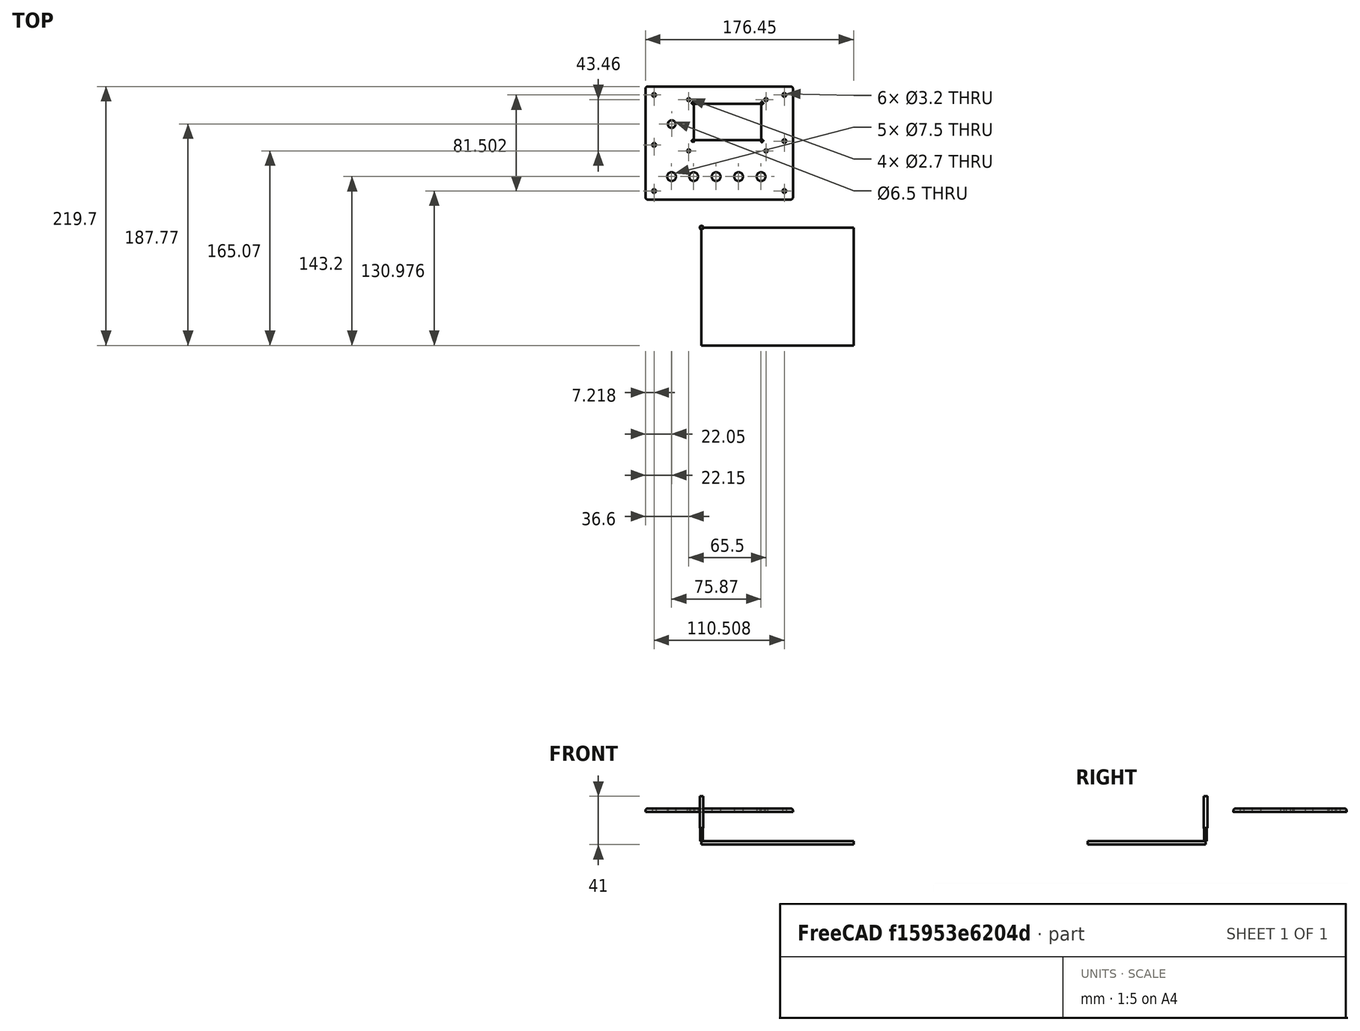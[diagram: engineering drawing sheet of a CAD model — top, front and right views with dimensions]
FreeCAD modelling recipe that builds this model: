
FCSTD DOCUMENT  (FreeCAD 0.21R33771 (Git))
Label: Top Plate CNC Job
License: All rights reserved
LicenseURL: http://en.wikipedia.org/wiki/All_rights_reserved
objects: Path::FeaturePython×5, Part::FeaturePython×3, App::DocumentObjectGroup×3, Part::Feature×1, App::Part×1, App::FeaturePython×1
note: 7 computed .brp shape members not serialized (recipe doc carries the construction recipe); baked Part::Feature solids carry a one-line shape summary decoded from their .brp

FEATURE [Part::Feature] Part__Feature  label="Top Plate"
  Placement = pos=(0,0,24.7) rot=(0,0,1;0rad)
  shape: bbox 125 x 96 x 3 mm, 50 faces (baked)
FEATURE [App::Part] Top_Enclosure_Plate  label="Top Enclosure Plate"
  Group = -> [Part__Feature]
  Origin = -> Origin
FEATURE [App::FeaturePython] SetupSheet  # Path/CAM operation (typed FeaturePython)
  ClearanceHeightExpression = OpStockZMax+SetupSheet.ClearanceHeightOffset
  ClearanceHeightOffset = 5
  CoolantMode = 0
  CoolantModes = None | Flood | Mist
  FinalDepthExpression = OpFinalDepth
  HorizRapid = 0
  SafeHeightExpression = OpStockZMax+SetupSheet.SafeHeightOffset
  SafeHeightOffset = 3
  StartDepthExpression = OpStartDepth
  StepDownExpression = OpToolDiameter
  VertRapid = 0
FEATURE [Part::FeaturePython] Clone  label="Model-Top Enclosure Plate"  # Draft clone (typed FeaturePython)
  AttacherType = Attacher::AttachEngine3D
  Fuse = false
  Objects = -> [Top_Enclosure_Plate]
  PathResource = Model
  Placement = pos=(49.4504,-121.7,-27.7) rot=(0,0,1;0rad)
  Scale = (1,1,1)
FEATURE [App::DocumentObjectGroup] Model
  Group = -> [Clone]
FEATURE [Part::FeaturePython] ToolBit  label="Endmill"  # Path/CAM toolbit (typed FeaturePython)
  BitPropertyNames = Chipload | CuttingEdgeHeight | Diameter | Flutes | Length | Material | ShankDiameter | SpindleDirection
  BitShape = C:/Program Files/FreeCAD 0.21/Mod\Path\Tools\Shape\endmill.fcstd
  Chipload = 0
  CuttingEdgeHeight = 11
  Diameter = 2
  Flutes = 0
  Length = 38
  Material = 0
  ShankDiameter = 3.1
  ShapeName = endmill
  SpindleDirection = 0
FEATURE [Path::FeaturePython] TC__Default_Tool  label="TC: EndMill01"  # Path/CAM operation (typed FeaturePython)
  HorizFeed = 5
  HorizRapid = 0
  SpindleDir = 0
  SpindleSpeed = 10000
  Tool = -> ToolBit
  ToolNumber = 10
  VertFeed = 2
  VertRapid = 0
  expr: HorizRapid = SetupSheet.HorizRapid
  expr: VertRapid = SetupSheet.VertRapid
FEATURE [App::DocumentObjectGroup] Tools
  Group = -> [TC__Default_Tool]
FEATURE [Part::FeaturePython] Stock001  # WARN: FeaturePython — macro-defined, semantics opaque (R4)
  Height = 3
  Length = 129
  Placement = pos=(0,-100,-3) rot=(0,0,1;0rad)
  StockType = CreateBox
  Width = 100
FEATURE [Path::FeaturePython] Pocket_Shape  label="Mounting & Bolt Holes"  # Path/CAM operation (typed FeaturePython)
  Active = true
  AreaParams:
    Tolerance = 1e-07
    FitArcs = True
    Simplify = False
    CleanDistance = 0.0
    Accuracy = 0.01
    Unit = 1.0
    MinArcPoints = 4
    MaxArcPoints = 100
    ClipperScale = 10000000.0
    Fill = 0
    Coplanar = 0
    Reorient = True
    Outline = False
    Explode = False
    OpenMode = 0
    Deflection = 0.01
    SubjectFill = 0
    ClipFill = 0
    Offset = 0.0
    ExtraPass = 0
    Stepover = 0.0
    LastStepover = 0.0
    JoinType = 0
    EndType = 0
    MiterLimit = 2.0
    RoundPrecision = 0.0
    PocketMode = 2
    ToolRadius = 1.0
    PocketExtraOffset = 0.0
    PocketStepover = 1.0
    PocketLastStepover = 0.0
    FromCenter = True
    Angle = 45.0
    AngleShift = 0.0
    Shift = 0.0
    Thicken = False
    SectionCount = -1
    Stepdown = 1.0
    SectionOffset = 0.0
    SectionTolerance = 1e-07
    SectionMode = 2
    Project = False
  Base = -> [Clone]
  ClearanceHeight = 5
  CoolantMode = 0
  CutMode = 0
  CycleTime = 00:10:06
  ExtensionCorners = true
  ExtensionLengthDefault = 1
  ExtraOffset = 0
  FinalDepth = -3
  FinishDepth = 0
  KeepToolDown = false
  MinTravel = false
  OffsetPattern = 1
  OpFinalDepth = -3
  OpStartDepth = 0
  OpStockZMax = 0
  OpStockZMin = -3
  OpToolDiameter = 2
  PathParams = {'orientation': 1, 'feedrate': 5.0, 'feedrate_v': 2.0, 'verbose': True, 'resume_height': 3.0, 'retraction': 5.0, 'return_end': True, 'preamble': False, 'start': Vector (119.15039579599825, -9.379392316911378, 5.0)}
  PocketLastStepOver = 0
  SafeHeight = 3
  SplitArcs = false
  StartAt = 0
  StartDepth = 0
  StartPoint = (0,0,0)
  StepDown = 2
  StepOver = 50
  ToolController = -> TC__Default_Tool
  UseOutline = false
  UseStartPoint = false
  ZigZagAngle = 45
  expr: ClearanceHeight = OpStockZMax + SetupSheet.ClearanceHeightOffset
  expr: ExtensionLengthDefault = OpToolDiameter / 2
  expr: FinalDepth = OpFinalDepth
  expr: SafeHeight = OpStockZMax + SetupSheet.SafeHeightOffset
  expr: StartDepth = OpStartDepth
  expr: StepDown = OpToolDiameter
FEATURE [Path::FeaturePython] Pocket_Shape001  label="Display Pocket"  # Path/CAM operation (typed FeaturePython)
  Active = true
  AreaParams:
    Tolerance = 1e-07
    FitArcs = True
    Simplify = False
    CleanDistance = 0.0
    Accuracy = 0.01
    Unit = 1.0
    MinArcPoints = 4
    MaxArcPoints = 100
    ClipperScale = 10000000.0
    Fill = 0
    Coplanar = 0
    Reorient = True
    Outline = False
    Explode = False
    OpenMode = 0
    Deflection = 0.01
    SubjectFill = 0
    ClipFill = 0
    Offset = 0.0
    ExtraPass = 0
    Stepover = 0.0
    LastStepover = 0.0
    JoinType = 0
    EndType = 0
    MiterLimit = 2.0
    RoundPrecision = 0.0
    PocketMode = 2
    ToolRadius = 1.0
    PocketExtraOffset = 0.0
    PocketStepover = 1.0
    PocketLastStepover = 0.0
    FromCenter = True
    Angle = 45.0
    AngleShift = 0.0
    Shift = 0.0
    Thicken = False
    SectionCount = -1
    Stepdown = 1.0
    SectionOffset = 0.0
    SectionTolerance = 1e-07
    SectionMode = 2
    Project = False
  Base = -> [Clone]
  ClearanceHeight = 5
  CoolantMode = 0
  CutMode = 0
  CycleTime = 00:15:16
  ExtensionCorners = true
  ExtensionLengthDefault = 1
  ExtraOffset = 0
  FinalDepth = -3
  FinishDepth = 0
  KeepToolDown = false
  MinTravel = false
  OffsetPattern = 1
  OpFinalDepth = -3
  OpStartDepth = 0
  OpStockZMax = 0
  OpStockZMin = -3
  OpToolDiameter = 2
  PathParams = {'orientation': 1, 'feedrate': 5.0, 'feedrate_v': 2.0, 'verbose': True, 'resume_height': 3.0, 'retraction': 5.0, 'return_end': True, 'preamble': False}
  PocketLastStepOver = 0
  SafeHeight = 3
  SplitArcs = false
  StartAt = 0
  StartDepth = 0
  StartPoint = (0,0,0)
  StepDown = 2
  StepOver = 50
  ToolController = -> TC__Default_Tool
  UseOutline = false
  UseStartPoint = false
  ZigZagAngle = 45
  expr: ClearanceHeight = OpStockZMax + SetupSheet.ClearanceHeightOffset
  expr: ExtensionLengthDefault = OpToolDiameter / 2
  expr: FinalDepth = OpFinalDepth
  expr: SafeHeight = OpStockZMax + SetupSheet.SafeHeightOffset
  expr: StartDepth = OpStartDepth
  expr: StepDown = OpToolDiameter
FEATURE [Path::FeaturePython] Profile  # Path/CAM operation (typed FeaturePython)
  Active = true
  AreaParams:
    Tolerance = 1e-07
    FitArcs = True
    Simplify = False
    CleanDistance = 0.0
    Accuracy = 0.01
    Unit = 1.0
    MinArcPoints = 4
    MaxArcPoints = 100
    ClipperScale = 10000000.0
    Fill = 0
    Coplanar = 0
    Reorient = True
    Outline = False
    Explode = False
    OpenMode = 0
    Deflection = 0.01
    SubjectFill = 0
    ClipFill = 0
    Offset = 1.0
    ExtraPass = 0
    Stepover = 0.0
    LastStepover = 0.0
    JoinType = 0
    EndType = 0
    MiterLimit = 2.0
    RoundPrecision = 0.0
    PocketMode = 0
    ToolRadius = 1.0
    PocketExtraOffset = 0.0
    PocketStepover = 0.0
    PocketLastStepover = 0.0
    FromCenter = False
    Angle = 45.0
    AngleShift = 0.0
    Shift = 0.0
    Thicken = False
    SectionCount = -1
    Stepdown = 1.0
    SectionOffset = 0.0
    SectionTolerance = 1e-07
    SectionMode = 2
    Project = False
  Base = -> [Clone]
  ClearanceHeight = 5
  CoolantMode = 0
  CycleTime = 00:03:32
  Direction = 0
  FinalDepth = -3
  HandleMultipleFeatures = 0
  JoinType = 0
  MiterLimit = 0.1
  OffsetExtra = 0
  OpFinalDepth = -3
  OpStartDepth = 0
  OpStockZMax = 0
  OpStockZMin = -3
  OpToolDiameter = 2
  PathParams = {'orientation': 1, 'feedrate': 5.0, 'feedrate_v': 2.0, 'verbose': True, 'resume_height': 3.0, 'retraction': 5.0, 'return_end': True, 'preamble': False}
  SafeHeight = 3
  Side = 0
  SplitArcs = false
  StartDepth = 0
  StartPoint = (0,0,0)
  StepDown = 2
  ToolController = -> TC__Default_Tool
  UseComp = true
  UseStartPoint = false
  processCircles = false
  processHoles = false
  processPerimeter = true
  expr: ClearanceHeight = OpStockZMax + SetupSheet.ClearanceHeightOffset
  expr: FinalDepth = OpFinalDepth
  expr: SafeHeight = OpStockZMax + SetupSheet.SafeHeightOffset
  expr: StartDepth = OpStartDepth
  expr: StepDown = OpToolDiameter
FEATURE [App::DocumentObjectGroup] Operations
  Group = -> [Pocket_Shape,Pocket_Shape001,Profile]
FEATURE [Path::FeaturePython] Job  # Path/CAM operation (typed FeaturePython)
  CycleTime = 00:28:54
  Fixtures = G54
  GeometryTolerance = 0.01
  JobType = 0
  LastPostProcessDate = 2024-08-13 14:29:16.978612
  LastPostProcessOutput = <userpath>\OneDrive\Github-projects\ElectricGuitarMK1\Research and Development\Interface Section\AFPI\Enclosure Design\Top Plate CNC Job.gcode
  Model = -> Model
  Operations = -> Operations
  OrderOutputBy = 0
  PostProcessor = 13
  PostProcessorOutputFile = %D/%d.gcode
  SetupSheet = -> SetupSheet
  SplitOutput = false
  Stock = -> Stock001
  Tools = -> Tools
